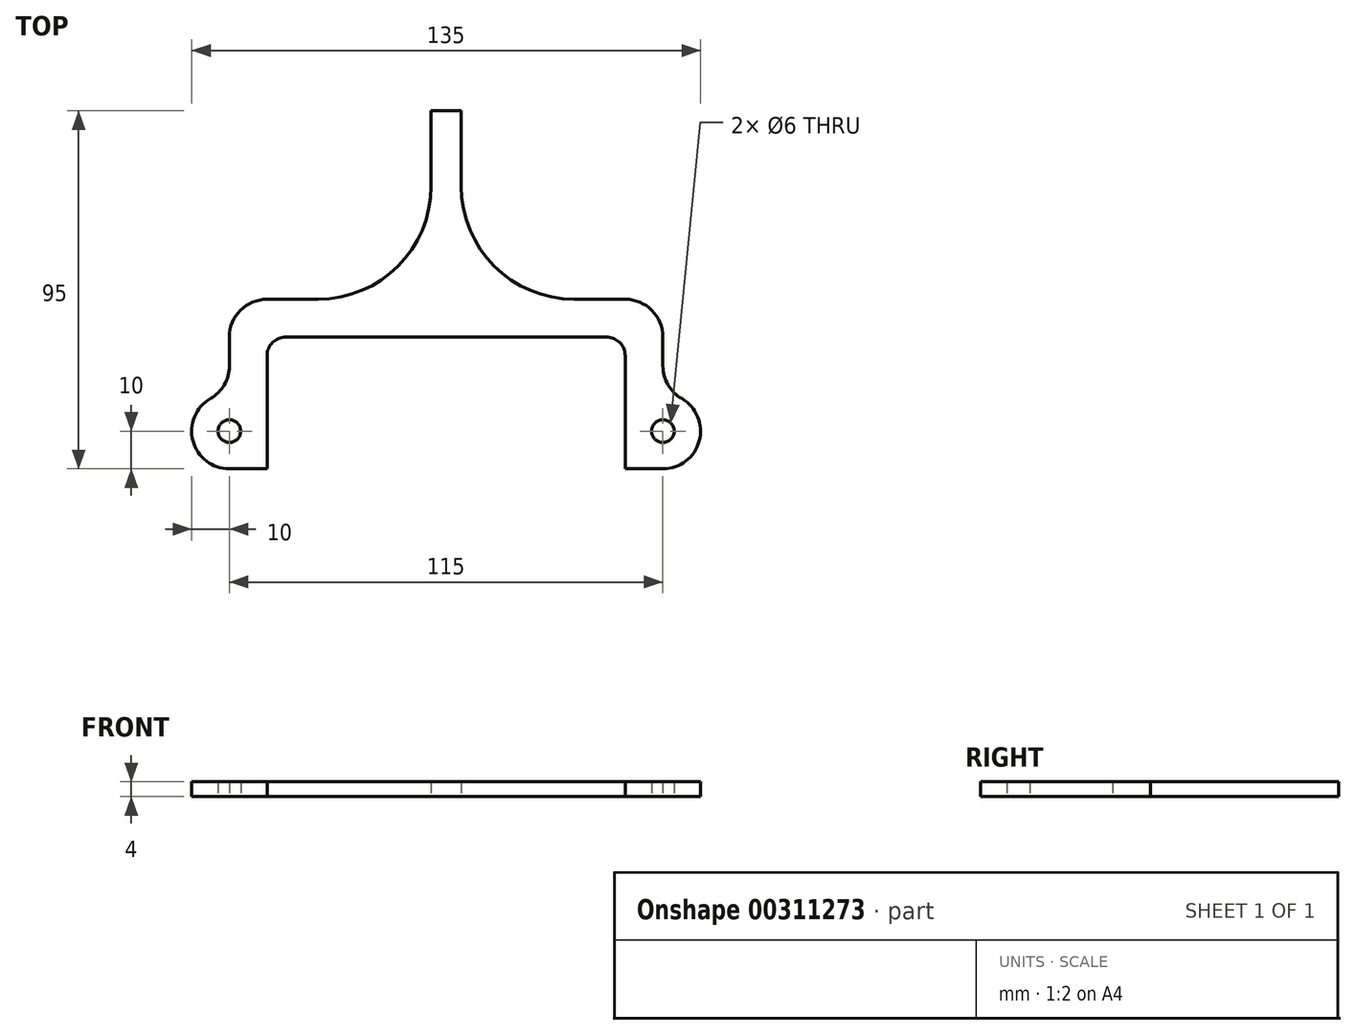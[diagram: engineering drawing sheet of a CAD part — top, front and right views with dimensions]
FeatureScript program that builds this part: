
annotation { "Feature Type Name" : "Feature", "Feature Type Description" : "" }
export const myFeature = defineFeature(function(context is Context, id is Id, definition is map)
    precondition{}
    {
        {
            var Q0;
            Q0=qCreatedBy(makeId("Top.planeOp"),FACE);
            var sketch = newSketch(context, id + "F0", { "sketchPlane" : qUnion([Q0])});
            skCircle(sketch, "E0", {"center": v(-57.5, 0) * mm, "radius": 3 * mm});
            skCircle(sketch, "E1", {"center": v(57.5, 0) * mm, "radius": 3 * mm});
            skLineSegment(sketch, "E2", {"start": v(-57.5, 0) * mm, "end": v(57.5, 0) * mm, "construction": true});
            skArc(sketch, "E3", {"start": v(-62.5, 8.66) * mm, "mid": v(-67.16, -2.59) * mm, "end": v(-57.5, -10) * mm});
            skArc(sketch, "E4", {"start": v(57.5, -10) * mm, "mid": v(67.16, -2.59) * mm, "end": v(62.5, 8.66) * mm});
            skLineSegment(sketch, "E5", {"start": v(-57.5, -10) * mm, "end": v(-47.5, -10) * mm});
            skLineSegment(sketch, "E6", {"start": v(-47.5, -10) * mm, "end": v(-47.5, 20) * mm});
            skLineSegment(sketch, "E7", {"start": v(-42.5, 25) * mm, "end": v(42.5, 25) * mm});
            skLineSegment(sketch, "E8", {"start": v(47.5, 20) * mm, "end": v(47.5, -10) * mm});
            skLineSegment(sketch, "E9", {"start": v(47.5, -10) * mm, "end": v(57.5, -10) * mm});
            skLineSegment(sketch, "E10", {"start": v(-4, 85) * mm, "end": v(4, 85) * mm});
            skPoint(sketch, "E11", {"position": v(0, 85) * mm});
            skLineSegment(sketch, "E12", {"start": v(-4, 85) * mm, "end": v(-4, 65) * mm});
            skLineSegment(sketch, "E13", {"start": v(4, 85) * mm, "end": v(4, 65) * mm});
            skLineSegment(sketch, "E14", {"start": v(-57.5, 17.32) * mm, "end": v(-57.5, 25) * mm});
            skLineSegment(sketch, "E15", {"start": v(-47.5, 35) * mm, "end": v(-34, 35) * mm});
            skLineSegment(sketch, "E16", {"start": v(34, 35) * mm, "end": v(47.5, 35) * mm});
            skLineSegment(sketch, "E17", {"start": v(57.5, 25) * mm, "end": v(57.5, 17.32) * mm});
            skPoint(sketch, "E18.visualSharp", {"position": v(-57.5, 35) * mm});
            skArc(sketch, "E18.filletArc", {"start": v(-47.5, 35) * mm, "mid": v(-54.57, 32.07) * mm, "end": v(-57.5, 25) * mm});
            skPoint(sketch, "E19.visualSharp", {"position": v(57.5, 35) * mm});
            skArc(sketch, "E19.filletArc", {"start": v(57.5, 25) * mm, "mid": v(54.57, 32.07) * mm, "end": v(47.5, 35) * mm});
            skPoint(sketch, "E20.visualSharp", {"position": v(-4, 35) * mm});
            skArc(sketch, "E20.filletArc", {"start": v(-34, 35) * mm, "mid": v(-12.79, 43.79) * mm, "end": v(-4, 65) * mm});
            skPoint(sketch, "E21.visualSharp", {"position": v(4, 35) * mm});
            skArc(sketch, "E21.filletArc", {"start": v(4, 65) * mm, "mid": v(12.79, 43.79) * mm, "end": v(34, 35) * mm});
            skPoint(sketch, "E22.visualSharp", {"position": v(-57.5, 10) * mm});
            skArc(sketch, "E22.filletArc", {"start": v(-62.5, 8.66) * mm, "mid": v(-58.84, 12.32) * mm, "end": v(-57.5, 17.32) * mm});
            skPoint(sketch, "E23.visualSharp", {"position": v(57.5, 10) * mm});
            skArc(sketch, "E23.filletArc", {"start": v(57.5, 17.32) * mm, "mid": v(58.84, 12.32) * mm, "end": v(62.5, 8.66) * mm});
            skArc(sketch, "E24.filletArc", {"start": v(-42.5, 25) * mm, "mid": v(-46.04, 23.54) * mm, "end": v(-47.5, 20) * mm});
            skArc(sketch, "E25.filletArc", {"start": v(47.5, 20) * mm, "mid": v(46.04, 23.54) * mm, "end": v(42.5, 25) * mm});
            skSolve(sketch);
        }
        {
            var Q0;
            Q0 = qSketchRegion(id + "F0", true);
            extrude(context, id + "F1", {"entities" : qUnion([Q0]), "depth" : 4 * mm});
        }
    });
